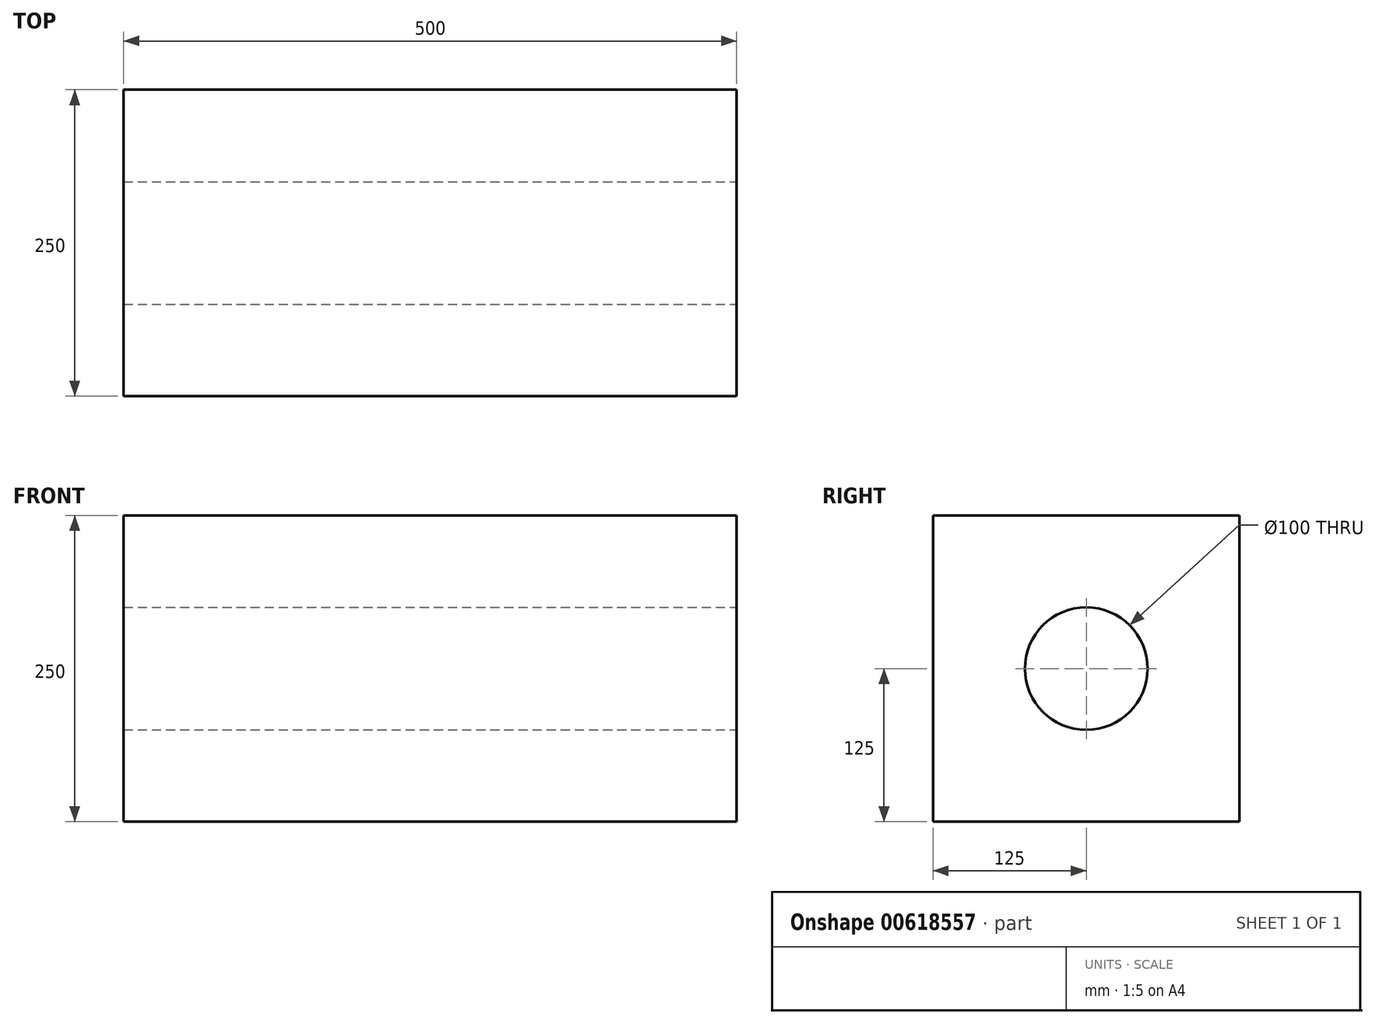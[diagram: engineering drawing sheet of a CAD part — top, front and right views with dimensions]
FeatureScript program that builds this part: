
annotation { "Feature Type Name" : "Feature", "Feature Type Description" : "" }
export const myFeature = defineFeature(function(context is Context, id is Id, definition is map)
    precondition{}
    {
        {
            var Q0;
            Q0=qCreatedBy(makeId("Top.planeOp"),FACE);
            var sketch = newSketch(context, id + "F0", { "sketchPlane" : qUnion([Q0])});
            skLineSegment(sketch, "E0.bottom", {"start": v(0, 0) * mm, "end": v(0, 0) * mm});
            skLineSegment(sketch, "E0.top", {"start": v(0, 0) * mm, "end": v(0, 0) * mm});
            skLineSegment(sketch, "E0.left", {"start": v(0, 0) * mm, "end": v(0, 0) * mm});
            skLineSegment(sketch, "E0.right", {"start": v(0, 0) * mm, "end": v(0, 0) * mm});
            skPoint(sketch, "E0.middle", {"position": v(0, 0) * mm});
            skLineSegment(sketch, "E1.bottom", {"start": v(250, 125) * mm, "end": v(-250, 125) * mm});
            skLineSegment(sketch, "E1.top", {"start": v(250, -125) * mm, "end": v(-250, -125) * mm});
            skLineSegment(sketch, "E1.left", {"start": v(250, 125) * mm, "end": v(250, -125) * mm});
            skLineSegment(sketch, "E1.right", {"start": v(-250, 125) * mm, "end": v(-250, -125) * mm});
            skSolve(sketch);
        }
        {
            var Q0;
            Q0=makeQuery(id+"F0.imprint","IMPRINT",FACE,{"disambiguationData":[TD([[makeQuery(id+"F0.imprint","IMPRINT",EDGE,{"derivedFrom":sQuery(id+"F0.wireOp",EDGE,"E1.bottom")}),1.0]])]});
            extrude(context, id + "F1", {"entities" : qUnion([Q0]), "oppositeDirection" : true, "depth" : 250 * mm, "offsetDistance" : 25 * mm});
        }
        {
            var Q0;
            Q0=makeQuery(id+"F1.opExtrude","SWEPT_FACE",FACE,{"disambiguationData":[OSD([sQuery(id+"F0.wireOp",EDGE,"E1.left")])]});
            var sketch = newSketch(context, id + "F2", { "sketchPlane" : qUnion([Q0])});
            skLineSegment(sketch, "E2.0", {"start": v(125, -125) * mm, "end": v(-125, -125) * mm});
            skLineSegment(sketch, "E3.0", {"start": v(0, -250) * mm, "end": v(0, 0) * mm});
            skCircle(sketch, "E4", {"center": v(0, -125) * mm, "radius": 50 * mm});
            skSolve(sketch);
        }
        {
            var Q0;
            {var subQ0=sQuery(id+"F2.wireOp",EDGE,"E4");var subQ1=sQuery(id+"F2.wireOp",EDGE,"E2.0");var subQ2=makeQuery(id+"F2.imprint","INTERSECT",VERTEX,{"disambiguationData":[OD(0.0)],"derivedFrom":[subQ1,subQ0]});Q0=makeQuery(id+"F2.imprint","IMPRINT",FACE,{"disambiguationData":[TD([[makeQuery(id+"F2.imprint","IMPRINT",EDGE,{"disambiguationData":[TD([[subQ2,-1.0]])],"derivedFrom":subQ1}),-1.0]])]});}
            var Q1;
            {var subQ0=sQuery(id+"F2.wireOp",EDGE,"E3.0");var subQ1=sQuery(id+"F2.wireOp",EDGE,"E2.0");var subQ2=makeQuery(id+"F2.imprint","INTERSECT",VERTEX,{"derivedFrom":[subQ1,subQ0]});Q1=makeQuery(id+"F2.imprint","IMPRINT",FACE,{"disambiguationData":[TD([[makeQuery(id+"F2.imprint","IMPRINT",EDGE,{"disambiguationData":[TD([[subQ2,-1.0]])],"derivedFrom":subQ1}),-1.0]])]});}
            var Q2;
            {var subQ0=sQuery(id+"F2.wireOp",EDGE,"E3.0");var subQ1=sQuery(id+"F2.wireOp",EDGE,"E2.0");var subQ2=makeQuery(id+"F2.imprint","INTERSECT",VERTEX,{"derivedFrom":[subQ1,subQ0]});Q2=makeQuery(id+"F2.imprint","IMPRINT",FACE,{"disambiguationData":[TD([[makeQuery(id+"F2.imprint","IMPRINT",EDGE,{"disambiguationData":[TD([[subQ2,-1.0]])],"derivedFrom":subQ1}),1.0]])]});}
            var Q3;
            {var subQ0=sQuery(id+"F2.wireOp",EDGE,"E4");var subQ1=sQuery(id+"F2.wireOp",EDGE,"E2.0");var subQ2=makeQuery(id+"F2.imprint","INTERSECT",VERTEX,{"disambiguationData":[OD(0.0)],"derivedFrom":[subQ1,subQ0]});Q3=makeQuery(id+"F2.imprint","IMPRINT",FACE,{"disambiguationData":[TD([[makeQuery(id+"F2.imprint","IMPRINT",EDGE,{"disambiguationData":[TD([[subQ2,-1.0]])],"derivedFrom":subQ1}),1.0]])]});}
            extrude(context, id + "F3", {"entities" : qUnion([Q0, Q1, Q2, Q3]), "operationType" : NewBodyOperationType.ADD, "oppositeDirection" : true, "depth" : 110.81 * mm, "offsetDistance" : 25 * mm});
        }
        {
            var Q0;
            Q0=makeQuery(id+"F1.opExtrude","SWEPT_FACE",FACE,{"disambiguationData":[OSD([sQuery(id+"F0.wireOp",EDGE,"E1.left")])]});
            var sketch = newSketch(context, id + "F4", { "sketchPlane" : qUnion([Q0])});
            skSolve(sketch);
        }
        {
            var Q0;
            {var subQ0=sQuery(id+"F0.wireOp",EDGE,"E1.left");Q0=makeQuery(id+"F4.imprint","IMPRINT",FACE,{"disambiguationData":[TD([[makeQuery(id+"F4.imprint","IMPRINT",EDGE,{"derivedFrom":makeQuery(id+"F1.opExtrude","CAP_EDGE",EDGE,{"disambiguationData":[OSD([subQ0])],"isStart":true})}),1.0]])]});}
            var sketch = newSketch(context, id + "F5", { "sketchPlane" : qUnion([Q0])});
            skLineSegment(sketch, "E5.0", {"start": v(125, -125) * mm, "end": v(-125, -125) * mm});
            skLineSegment(sketch, "E6.0", {"start": v(0, -250) * mm, "end": v(0, 0) * mm});
            skPoint(sketch, "E7", {"position": v(0, -125) * mm});
            skSolve(sketch);
        }
        {
            var Q0;
            Q0=sQuery(id+"F5.wireOp",VERTEX,"E7");
            var Q1;
            Q1=makeQuery(id+"F1.opExtrude","SWEPT_BODY",BODY,{"disambiguationData":[OSD([sQuery(id+"F0.wireOp",EDGE,"E1.bottom"),sQuery(id+"F0.wireOp",EDGE,"E1.top"),sQuery(id+"F0.wireOp",EDGE,"E1.left"),sQuery(id+"F0.wireOp",EDGE,"E1.right")])]});
            hole(context, id + "F6", {"style" : HoleStyle.SIMPLE, "endStyle" : HoleEndStyle.THROUGH, "holeDiameter" : 100 * mm, "majorDiameter" : 5 * mm, "isTappedThrough" : true, "tappedDepth" : 12 * mm, "tapClearance" : 3, "locations" : qUnion([Q0]), "scope" : qUnion([Q1])});
        }
    });
